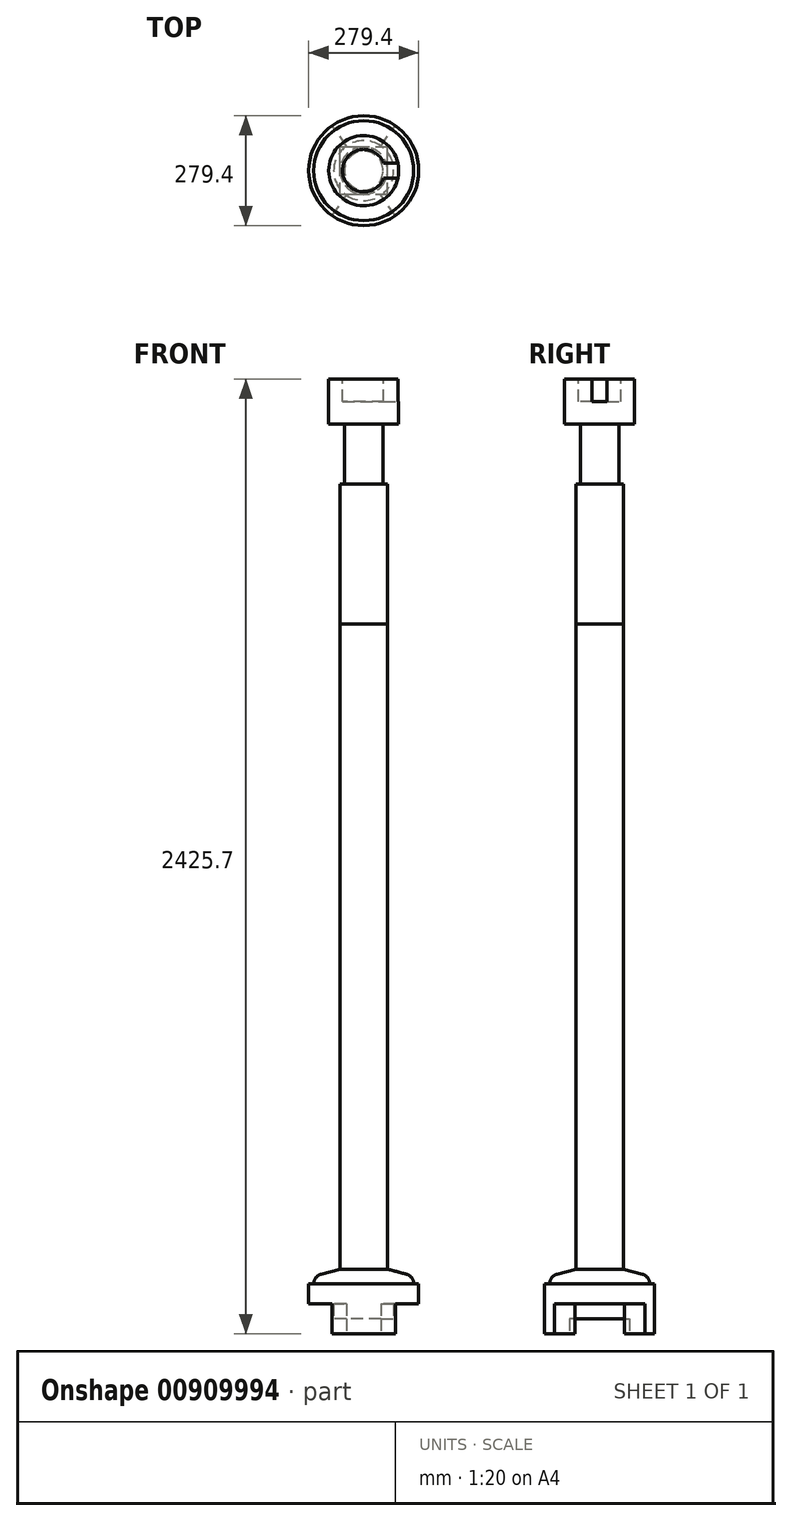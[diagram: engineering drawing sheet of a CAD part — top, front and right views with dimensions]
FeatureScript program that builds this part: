
annotation { "Feature Type Name" : "Feature", "Feature Type Description" : "" }
export const myFeature = defineFeature(function(context is Context, id is Id, definition is map)
    precondition{}
    {
        {
            var Q0;
            Q0=qCreatedBy(makeId("Front.planeOp"),FACE);
            var sketch = newSketch(context, id + "F0", { "sketchPlane" : qUnion([Q0])});
            skLineSegment(sketch, "E0", {"start": v(0, 0) * mm, "end": v(139.7, 0) * mm});
            skLineSegment(sketch, "E1", {"start": v(139.7, 0) * mm, "end": v(139.7, 127) * mm});
            skLineSegment(sketch, "E2", {"start": v(139.7, 127) * mm, "end": v(127, 127) * mm});
            skArc(sketch, "E3", {"start": v(127, 127) * mm, "mid": v(121.75, 142.46) * mm, "end": v(108.17, 151.53) * mm});
            skLineSegment(sketch, "E4", {"start": v(108.17, 151.53) * mm, "end": v(60.32, 164.36) * mm});
            skLineSegment(sketch, "E5", {"start": v(60.32, 164.36) * mm, "end": v(60.32, 1803.4) * mm});
            skLineSegment(sketch, "E6", {"start": v(60.32, 1803.4) * mm, "end": v(0, 1803.4) * mm});
            skLineSegment(sketch, "E7", {"start": v(0, 1803.4) * mm, "end": v(0, 0) * mm});
            skLineSegment(sketch, "E8", {"start": v(60.32, 1803.4) * mm, "end": v(60.32, 2159) * mm});
            skLineSegment(sketch, "E9", {"start": v(60.32, 2159) * mm, "end": v(-60.32, 2159) * mm});
            skLineSegment(sketch, "E10", {"start": v(-60.32, 2159) * mm, "end": v(-60.32, 1803.4) * mm});
            skLineSegment(sketch, "E11", {"start": v(-60.32, 1803.4) * mm, "end": v(0, 1803.4) * mm});
            skLineSegment(sketch, "E12", {"start": v(49.21, 2159) * mm, "end": v(49.21, 2311.4) * mm});
            skLineSegment(sketch, "E13", {"start": v(0, 2368.55) * mm, "end": v(0, 2159) * mm});
            skLineSegment(sketch, "E14", {"start": v(53.97, 2425.7) * mm, "end": v(88.9, 2425.7) * mm});
            skLineSegment(sketch, "E15", {"start": v(88.9, 2425.7) * mm, "end": v(88.9, 2311.4) * mm});
            skLineSegment(sketch, "E16", {"start": v(88.9, 2311.4) * mm, "end": v(49.21, 2311.4) * mm});
            skLineSegment(sketch, "E17", {"start": v(53.97, 2425.7) * mm, "end": v(53.97, 2368.55) * mm});
            skLineSegment(sketch, "E18", {"start": v(53.97, 2368.55) * mm, "end": v(0, 2368.55) * mm});
            skSolve(sketch);
        }
        {
            var Q0;
            Q0=makeQuery(id+"F0.imprint","IMPRINT",FACE,{"disambiguationData":[TD([[makeQuery(id+"F0.imprint","IMPRINT",EDGE,{"derivedFrom":sQuery(id+"F0.wireOp",EDGE,"E0")}),1.0]])]});
            var Q1;
            Q1=sQuery(id+"F0.wireOp",EDGE,"E7");
            revolve(context, id + "F1", {"surfaceOperationType" : NewSurfaceOperationType.NEW, "entities" : qUnion([Q0]), "axis" : qUnion([Q1]), "revolveType" : RevolveType.FULL});
        }
        {
            var Q0;
            Q0=makeQuery(id+"F1.opRevolve","SWEPT_FACE",FACE,{"disambiguationData":[OSD([sQuery(id+"F0.wireOp",EDGE,"E0")])]});
            var sketch = newSketch(context, id + "F2", { "sketchPlane" : qUnion([Q0])});
            skCircle(sketch, "E19", {"center": v(0, 0) * mm, "radius": 76.2 * mm});
            skLineSegment(sketch, "E20", {"start": v(-80.13, 114.44) * mm, "end": v(-43.7, 62.42) * mm});
            skLineSegment(sketch, "E21", {"start": v(80.13, 114.44) * mm, "end": v(43.7, 62.42) * mm});
            skLineSegment(sketch, "E22", {"start": v(0, 0) * mm, "end": v(0, 139.7) * mm, "construction": true});
            skCircle(sketch, "E23", {"center": v(0, 0) * mm, "radius": 139.7 * mm});
            skLineSegment(sketch, "E24.trimOffspring", {"start": v(43.7, -62.42) * mm, "end": v(80.13, -114.44) * mm});
            skLineSegment(sketch, "E25.trimOffspring", {"start": v(-43.7, -62.42) * mm, "end": v(-80.13, -114.44) * mm});
            skSolve(sketch);
        }
        {
            var Q0;
            {var subQ0=sQuery(id+"F2.wireOp",EDGE,"E19");var subQ1=makeQuery(id+"F2.imprint","INTERSECT",VERTEX,{"derivedFrom":[subQ0,sQuery(id+"F2.wireOp",EDGE,"E20")]});Q0=makeQuery(id+"F2.imprint","IMPRINT",FACE,{"disambiguationData":[TD([[makeQuery(id+"F2.imprint","IMPRINT",EDGE,{"disambiguationData":[TD([[subQ1,1.0]])],"derivedFrom":subQ0}),1.0]])]});}
            extrude(context, id + "F3", {"entities" : qUnion([Q0]), "operationType" : NewBodyOperationType.REMOVE, "oppositeDirection" : true, "depth" : 38.1 * mm, "offsetDistance" : 25 * mm});
        }
        {
            var Q0;
            {var subQ0=sQuery(id+"F2.wireOp",EDGE,"E20");Q0=makeQuery(id+"F2.imprint","IMPRINT",FACE,{"disambiguationData":[TD([[makeQuery(id+"F2.imprint","IMPRINT",EDGE,{"derivedFrom":subQ0}),-1.0]])]});}
            var Q1;
            {var subQ0=sQuery(id+"F2.wireOp",EDGE,"E21");Q1=makeQuery(id+"F2.imprint","IMPRINT",FACE,{"disambiguationData":[TD([[makeQuery(id+"F2.imprint","IMPRINT",EDGE,{"derivedFrom":subQ0}),1.0]])]});}
            extrude(context, id + "F4", {"entities" : qUnion([Q0, Q1]), "operationType" : NewBodyOperationType.REMOVE, "oppositeDirection" : true, "depth" : 76.2 * mm, "offsetDistance" : 25 * mm});
        }
        {
            var Q0;
            Q0=makeQuery(id+"F0.imprint","IMPRINT",FACE,{"disambiguationData":[TD([[makeQuery(id+"F0.imprint","IMPRINT",EDGE,{"derivedFrom":sQuery(id+"F0.wireOp",EDGE,"E6")}),-1.0]])]});
            extrude(context, id + "F5", {"entities" : qUnion([Q0]), "operationType" : NewBodyOperationType.ADD, "depth" : 120.65 * mm, "offsetDistance" : 25 * mm, "symmetric" : true});
        }
        {
            var Q0;
            {var subQ0=sQuery(id+"F0.wireOp",EDGE,"E12");Q0=makeQuery(id+"F0.imprint","IMPRINT",FACE,{"disambiguationData":[TD([[makeQuery(id+"F0.imprint","IMPRINT",EDGE,{"derivedFrom":subQ0}),1.0]])]});}
            var Q1;
            Q1=sQuery(id+"F0.wireOp",EDGE,"E13");
            revolve(context, id + "F6", {"operationType" : NewBodyOperationType.ADD, "surfaceOperationType" : NewSurfaceOperationType.NEW, "entities" : qUnion([Q0]), "axis" : qUnion([Q1]), "revolveType" : RevolveType.FULL});
        }
        {
            var Q0;
            Q0=makeQuery(id+"F6.opRevolve","SWEPT_FACE",FACE,{"disambiguationData":[OSD([sQuery(id+"F0.wireOp",EDGE,"E14")])]});
            var sketch = newSketch(context, id + "F7", { "sketchPlane" : qUnion([Q0])});
            skLineSegment(sketch, "E26.bottom", {"start": v(0, -19.05) * mm, "end": v(88.9, -19.05) * mm});
            skLineSegment(sketch, "E26.top", {"start": v(0, 19.05) * mm, "end": v(88.9, 19.05) * mm});
            skLineSegment(sketch, "E26.left", {"start": v(0, -19.05) * mm, "end": v(0, 19.05) * mm});
            skLineSegment(sketch, "E26.right", {"start": v(88.9, -19.05) * mm, "end": v(88.9, 19.05) * mm});
            skLineSegment(sketch, "E27", {"start": v(0, 0) * mm, "end": v(88.9, 0) * mm, "construction": true});
            skSolve(sketch);
        }
        {
            var Q0;
            {var subQ0=sQuery(id+"F7.wireOp",EDGE,"E26.bottom");var subQ1=sQuery(id+"F0.wireOp",EDGE,"E14");var subQ2=makeQuery(id+"F6.opRevolve","SWEPT_EDGE",EDGE,{"disambiguationData":[OSD([subQ1,sQuery(id+"F0.wireOp",EDGE,"E15")])]});var subQ3=makeQuery(id+"F7.imprint","INTERSECT",VERTEX,{"derivedFrom":[subQ2,subQ0]});Q0=makeQuery(id+"F7.imprint","IMPRINT",FACE,{"disambiguationData":[TD([[makeQuery(id+"F7.imprint","IMPRINT",EDGE,{"disambiguationData":[TD([[subQ3,1.0]])],"derivedFrom":subQ0}),1.0]])]});}
            var Q1;
            Q1=makeQuery(id+"F6.opRevolve","SWEPT_FACE",FACE,{"disambiguationData":[OSD([sQuery(id+"F0.wireOp",EDGE,"E18")])]});
            extrude(context, id + "F8", {"entities" : qUnion([Q0]), "operationType" : NewBodyOperationType.REMOVE, "endBound" : BoundingType.UP_TO_SURFACE, "oppositeDirection" : true, "depth" : 25 * mm, "endBoundEntityFace" : qUnion([Q1]), "offsetDistance" : 25 * mm});
        }
    });
